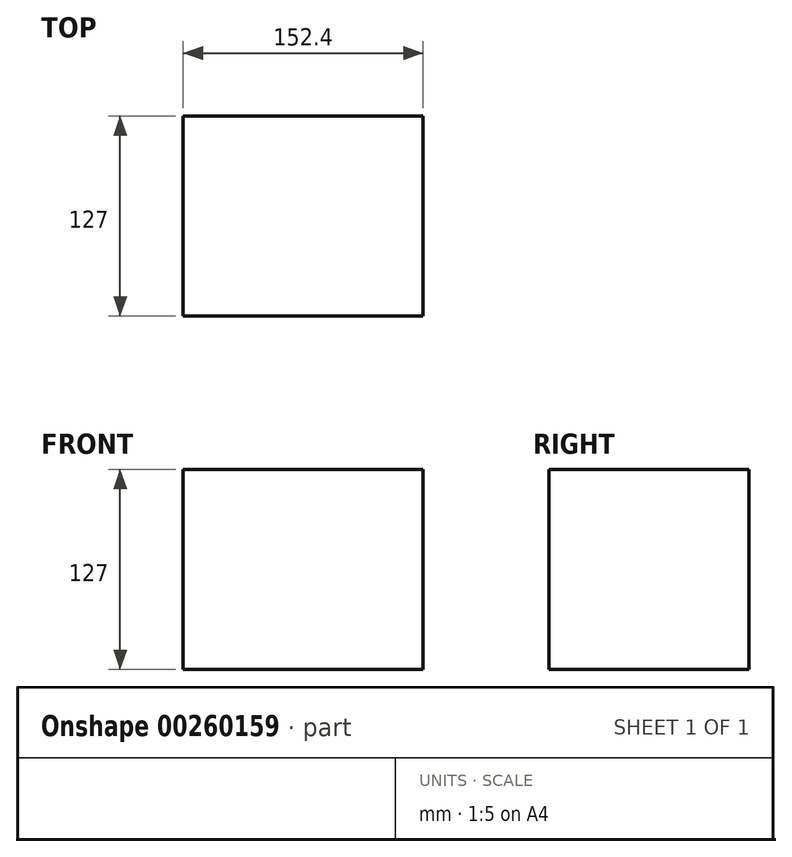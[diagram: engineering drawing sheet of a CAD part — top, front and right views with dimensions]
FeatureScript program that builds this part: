
annotation { "Feature Type Name" : "Feature", "Feature Type Description" : "" }
export const myFeature = defineFeature(function(context is Context, id is Id, definition is map)
    precondition{}
    {
        {
            var Q0;
            Q0=qCreatedBy(makeId("Top.planeOp"),FACE);
            var sketch = newSketch(context, id + "F0", { "sketchPlane" : qUnion([Q0])});
            skLineSegment(sketch, "E0.bottom", {"start": v(76.2, -63.5) * mm, "end": v(-76.2, -63.5) * mm});
            skLineSegment(sketch, "E0.top", {"start": v(76.2, 63.5) * mm, "end": v(-76.2, 63.5) * mm});
            skLineSegment(sketch, "E0.left", {"start": v(76.2, -63.5) * mm, "end": v(76.2, 63.5) * mm});
            skLineSegment(sketch, "E0.right", {"start": v(-76.2, -63.5) * mm, "end": v(-76.2, 63.5) * mm});
            skPoint(sketch, "E0.middle", {"position": v(0, 0) * mm});
            skSolve(sketch);
        }
        {
            var Q0;
            Q0 = qSketchRegion(id + "F0", true);
            extrude(context, id + "F1", {"entities" : qUnion([Q0]), "depth" : 127 * mm});
        }
    });
